# Revit family: Haworth_Epure_MeetingTop_EU_PRELIMINARY
name_source: partatom
category: Furniture
units: mm (PartAtom-declared; Revit-internal decimal feet)

## family parameters
Always vertical = Yes
Cut with Voids When Loaded = No
OmniClass Number = 23.40.70.14.64.11
OmniClass Title = Office Furniture
Room Calculation Point = No
Shared = No
Work Plane-Based = No

## types (9) — shared parameters
Actual Height = 73 cm
Assembly Code = E2020200
Description = Haworth - Epure - Meeting Top
Leg Height = 70 cm
Manufacturer = Haworth
Model = EUMXTXXXX
Revision Number = 1
Size = Verify Final Dim.w/ Haworth
URL = https://www.haworth.com
URL - Product = https://www.haworth.com
Warranty = http://www.haworth.com

## per-type parameters (varying)
| type | Actual Depth | Actual Width |
| 70 x 70 - Rectangular | 70 cm | 70 cm |
| 140 x 70 - Half-moon | 70 cm | 140 cm |
| 140 x 70 - Rectangular | 70 cm | 140 cm |
| 200 x 100 - Barrel | 100 cm | 200 cm |
| 210 x 70 - Rectangular | 70 cm | 210 cm |
| 240 x 120 - Barrel | 120 cm | 240 cm |
| 70 x 70 - 1/4 Elliptical | 70 cm | 70 cm |
| 70 x 70 - 45Deg Linking | 70 cm | 70 cm |
| 70 x 70 - 90Deg Linking | 70 cm | 70 cm |

type visibility flags: 9 boolean params named "<type name>" — each type sets only its own to Yes (folded from table)

## geometry (parser evidence)
native form markers: Sweep x4
no freeform markers — native parametric forms only
